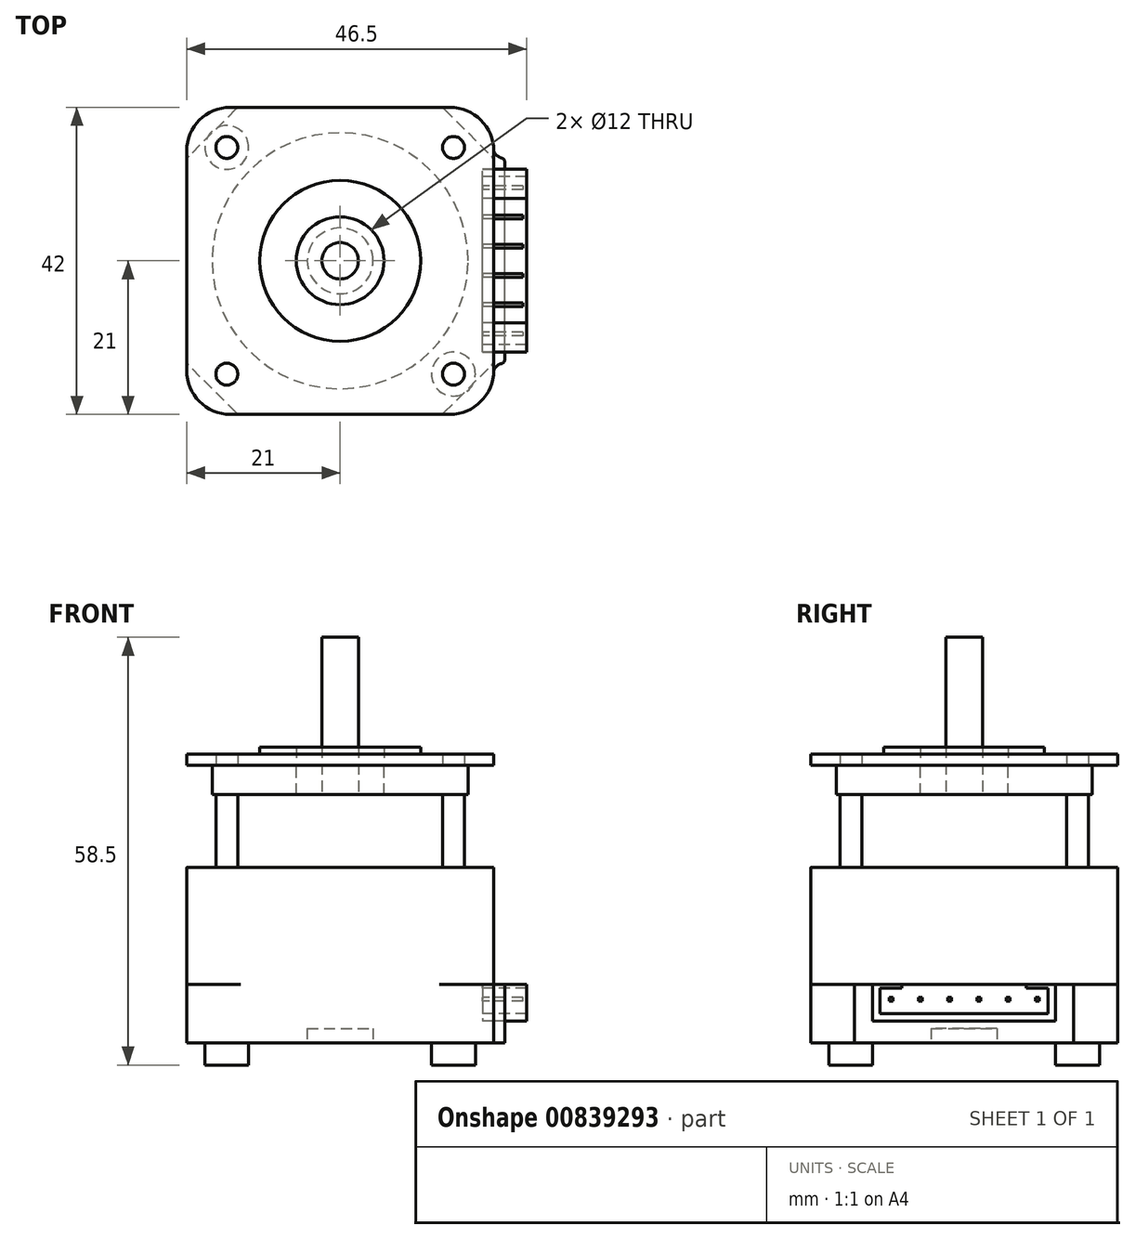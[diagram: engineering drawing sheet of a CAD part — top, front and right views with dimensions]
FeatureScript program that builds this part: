
annotation { "Feature Type Name" : "Feature", "Feature Type Description" : "" }
export const myFeature = defineFeature(function(context is Context, id is Id, definition is map)
    precondition{}
    {
        {
            var Q0;
            Q0=qCreatedBy(makeId("Top.planeOp"),FACE);
            var sketch = newSketch(context, id + "F0", { "sketchPlane" : qUnion([Q0])});
            skLineSegment(sketch, "E0.bottom", {"start": v(21, 21) * mm, "end": v(-21, 21) * mm});
            skLineSegment(sketch, "E0.top", {"start": v(21, -21) * mm, "end": v(-21, -21) * mm});
            skLineSegment(sketch, "E0.left", {"start": v(21, 21) * mm, "end": v(21, -21) * mm});
            skLineSegment(sketch, "E0.right", {"start": v(-21, 21) * mm, "end": v(-21, -21) * mm});
            skPoint(sketch, "E0.middle", {"position": v(0, 0) * mm});
            skLineSegment(sketch, "E1", {"start": v(-14, 21) * mm, "end": v(-21, 14) * mm});
            skLineSegment(sketch, "E2.MirrorCS", {"start": v(14, 21) * mm, "end": v(21, 14) * mm});
            skLineSegment(sketch, "E3.MirrorCS", {"start": v(-14, -21) * mm, "end": v(-21, -14) * mm});
            skLineSegment(sketch, "E4.MirrorCS", {"start": v(14, -21) * mm, "end": v(21, -14) * mm});
            skSolve(sketch);
        }
        {
            var Q0;
            {var subQ0=sQuery(id+"F0.wireOp",EDGE,"E1");Q0=makeQuery(id+"F0.imprint","IMPRINT",FACE,{"disambiguationData":[TD([[makeQuery(id+"F0.imprint","IMPRINT",EDGE,{"derivedFrom":subQ0}),1.0]])]});}
            extrude(context, id + "F1", {"entities" : qUnion([Q0]), "endBound" : BoundingType.SYMMETRIC, "depth" : 18 * mm, "offsetDistance" : 25 * mm});
        }
        {
            var Q0;
            Q0=makeQuery(id+"F1.opExtrude","SWEPT_EDGE",EDGE,{"disambiguationData":[OSD([sQuery(id+"F0.wireOp",EDGE,"E0.right"),sQuery(id+"F0.wireOp",EDGE,"E3.MirrorCS")])]});
            var Q1;
            Q1=makeQuery(id+"F1.opExtrude","SWEPT_EDGE",EDGE,{"disambiguationData":[OSD([sQuery(id+"F0.wireOp",EDGE,"E0.top"),sQuery(id+"F0.wireOp",EDGE,"E3.MirrorCS")])]});
            var Q2;
            Q2=makeQuery(id+"F1.opExtrude","SWEPT_EDGE",EDGE,{"disambiguationData":[OSD([sQuery(id+"F0.wireOp",EDGE,"E0.top"),sQuery(id+"F0.wireOp",EDGE,"E4.MirrorCS")])]});
            var Q3;
            Q3=makeQuery(id+"F1.opExtrude","SWEPT_EDGE",EDGE,{"disambiguationData":[OSD([sQuery(id+"F0.wireOp",EDGE,"E0.left"),sQuery(id+"F0.wireOp",EDGE,"E4.MirrorCS")])]});
            var Q4;
            Q4=makeQuery(id+"F1.opExtrude","SWEPT_EDGE",EDGE,{"disambiguationData":[OSD([sQuery(id+"F0.wireOp",EDGE,"E0.left"),sQuery(id+"F0.wireOp",EDGE,"E2.MirrorCS")])]});
            var Q5;
            Q5=makeQuery(id+"F1.opExtrude","SWEPT_EDGE",EDGE,{"disambiguationData":[OSD([sQuery(id+"F0.wireOp",EDGE,"E0.bottom"),sQuery(id+"F0.wireOp",EDGE,"E2.MirrorCS")])]});
            var Q6;
            Q6=makeQuery(id+"F1.opExtrude","SWEPT_EDGE",EDGE,{"disambiguationData":[OSD([sQuery(id+"F0.wireOp",EDGE,"E0.bottom"),sQuery(id+"F0.wireOp",EDGE,"E1")])]});
            var Q7;
            Q7=makeQuery(id+"F1.opExtrude","SWEPT_EDGE",EDGE,{"disambiguationData":[OSD([sQuery(id+"F0.wireOp",EDGE,"E0.right"),sQuery(id+"F0.wireOp",EDGE,"E1")])]});
            fillet(context, id + "F2", {"entities" : qUnion([Q0, Q1, Q2, Q3, Q4, Q5, Q6, Q7]), "radius" : 1 * mm, "tangentPropagation" : true, "allowEdgeOverflow" : false});
        }
        {
            var Q0;
            Q0=makeQuery(id+"F1.opExtrude","CAP_FACE",FACE,{"disambiguationData":[OSD([sQuery(id+"F0.wireOp",EDGE,"E0.bottom"),sQuery(id+"F0.wireOp",EDGE,"E0.top"),sQuery(id+"F0.wireOp",EDGE,"E0.left"),sQuery(id+"F0.wireOp",EDGE,"E0.right"),sQuery(id+"F0.wireOp",EDGE,"E1"),sQuery(id+"F0.wireOp",EDGE,"E2.MirrorCS"),sQuery(id+"F0.wireOp",EDGE,"E3.MirrorCS"),sQuery(id+"F0.wireOp",EDGE,"E4.MirrorCS")])],"isStart":true});
            var sketch = newSketch(context, id + "F3", { "sketchPlane" : qUnion([Q0])});
            skLineSegment(sketch, "E5.bottom", {"start": v(-21, 21) * mm, "end": v(21, 21) * mm});
            skLineSegment(sketch, "E5.top", {"start": v(-21, -21) * mm, "end": v(21, -21) * mm});
            skLineSegment(sketch, "E5.left", {"start": v(-21, 21) * mm, "end": v(-21, -21) * mm});
            skLineSegment(sketch, "E5.right", {"start": v(21, 21) * mm, "end": v(21, -21) * mm});
            skPoint(sketch, "E5.middle", {"position": v(0, 0) * mm});
            skLineSegment(sketch, "E6", {"start": v(21, 14) * mm, "end": v(22.5, 14) * mm});
            skLineSegment(sketch, "E7.MirrorCS", {"start": v(21, -14) * mm, "end": v(22.5, -14) * mm});
            skLineSegment(sketch, "E8", {"start": v(22.5, 14) * mm, "end": v(22.5, -14) * mm});
            skArc(sketch, "E9", {"start": v(21, 15) * mm, "mid": v(21.6, 14.27) * mm, "end": v(22.5, 14) * mm});
            skArc(sketch, "E10.MirrorCS", {"start": v(21, -15) * mm, "mid": v(21.6, -14.27) * mm, "end": v(22.5, -14) * mm});
            skSolve(sketch);
        }
        {
            var Q0;
            {var subQ3=sQuery(id+"F0.wireOp",EDGE,"E1");Q0=makeQuery(id+"F3.imprint","IMPRINT",FACE,{"disambiguationData":[TD([[makeQuery(id+"F3.imprint","IMPRINT",EDGE,{"derivedFrom":makeQuery(id+"F1.opExtrude","CAP_EDGE",EDGE,{"disambiguationData":[OSD([subQ3])],"isStart":true})}),-1.0]])]});}
            var Q1;
            {var subQ0=sQuery(id+"F0.wireOp",EDGE,"E2.MirrorCS");Q1=makeQuery(id+"F3.imprint","IMPRINT",FACE,{"disambiguationData":[TD([[makeQuery(id+"F3.imprint","IMPRINT",EDGE,{"derivedFrom":makeQuery(id+"F1.opExtrude","CAP_EDGE",EDGE,{"disambiguationData":[OSD([subQ0])],"isStart":true})}),-1.0]])]});}
            var Q2;
            {var subQ0=sQuery(id+"F0.wireOp",EDGE,"E3.MirrorCS");Q2=makeQuery(id+"F3.imprint","IMPRINT",FACE,{"disambiguationData":[TD([[makeQuery(id+"F3.imprint","IMPRINT",EDGE,{"derivedFrom":makeQuery(id+"F1.opExtrude","CAP_EDGE",EDGE,{"disambiguationData":[OSD([subQ0])],"isStart":true})}),-1.0]])]});}
            var Q3;
            {var subQ0=sQuery(id+"F0.wireOp",EDGE,"E4.MirrorCS");Q3=makeQuery(id+"F3.imprint","IMPRINT",FACE,{"disambiguationData":[TD([[makeQuery(id+"F3.imprint","IMPRINT",EDGE,{"derivedFrom":makeQuery(id+"F1.opExtrude","CAP_EDGE",EDGE,{"disambiguationData":[OSD([subQ0])],"isStart":true})}),1.0]])]});}
            var Q4;
            {var subQ0=sQuery(id+"F0.wireOp",EDGE,"E1");Q4=makeQuery(id+"F3.imprint","IMPRINT",FACE,{"disambiguationData":[TD([[makeQuery(id+"F3.imprint","IMPRINT",EDGE,{"derivedFrom":makeQuery(id+"F1.opExtrude","CAP_EDGE",EDGE,{"disambiguationData":[OSD([subQ0])],"isStart":true})}),1.0]])]});}
            var Q5;
            {var subQ0=sQuery(id+"F3.wireOp",EDGE,"E6");Q5=makeQuery(id+"F3.imprint","IMPRINT",FACE,{"disambiguationData":[TD([[makeQuery(id+"F3.imprint","IMPRINT",EDGE,{"derivedFrom":subQ0}),-1.0]])]});}
            var Q6;
            {var subQ0=sQuery(id+"F3.wireOp",EDGE,"E6");Q6=makeQuery(id+"F3.imprint","IMPRINT",FACE,{"disambiguationData":[TD([[makeQuery(id+"F3.imprint","IMPRINT",EDGE,{"derivedFrom":subQ0}),1.0]])]});}
            var Q7;
            {var subQ0=sQuery(id+"F3.wireOp",EDGE,"E7.MirrorCS");Q7=makeQuery(id+"F3.imprint","IMPRINT",FACE,{"disambiguationData":[TD([[makeQuery(id+"F3.imprint","IMPRINT",EDGE,{"derivedFrom":subQ0}),-1.0]])]});}
            extrude(context, id + "F4", {"entities" : qUnion([Q0, Q1, Q2, Q3, Q4, Q5, Q6, Q7]), "operationType" : NewBodyOperationType.ADD, "depth" : 11 * mm, "offsetDistance" : 25 * mm});
        }
        {
            var Q0;
            Q0=makeQuery(id+"F4.opExtrude","SWEPT_EDGE",EDGE,{"disambiguationData":[OSD([sQuery(id+"F3.wireOp",EDGE,"E5.bottom"),sQuery(id+"F3.wireOp",EDGE,"E5.right")])]});
            var Q1;
            Q1=makeQuery(id+"F4.opExtrude","SWEPT_EDGE",EDGE,{"disambiguationData":[OSD([sQuery(id+"F3.wireOp",EDGE,"E5.top"),sQuery(id+"F3.wireOp",EDGE,"E5.right")])]});
            var Q2;
            Q2=makeQuery(id+"F4.opExtrude","SWEPT_EDGE",EDGE,{"disambiguationData":[OSD([sQuery(id+"F3.wireOp",EDGE,"E5.top"),sQuery(id+"F3.wireOp",EDGE,"E5.left")])]});
            var Q3;
            Q3=makeQuery(id+"F4.opExtrude","SWEPT_EDGE",EDGE,{"disambiguationData":[OSD([sQuery(id+"F3.wireOp",EDGE,"E5.bottom"),sQuery(id+"F3.wireOp",EDGE,"E5.left")])]});
            fillet(context, id + "F5", {"entities" : qUnion([Q0, Q1, Q2, Q3]), "radius" : 6 * mm, "tangentPropagation" : true, "allowEdgeOverflow" : false});
        }
        {
            var Q0;
            Q0=makeQuery(id+"F4.opExtrude","SWEPT_EDGE",EDGE,{"disambiguationData":[OSD([sQuery(id+"F3.wireOp",EDGE,"E6"),sQuery(id+"F3.wireOp",EDGE,"E8"),sQuery(id+"F3.wireOp",EDGE,"E9")])]});
            var Q1;
            Q1=makeQuery(id+"F4.opExtrude","SWEPT_EDGE",EDGE,{"disambiguationData":[OSD([sQuery(id+"F3.wireOp",EDGE,"E7.MirrorCS"),sQuery(id+"F3.wireOp",EDGE,"E8"),sQuery(id+"F3.wireOp",EDGE,"E10.MirrorCS")])]});
            fillet(context, id + "F6", {"entities" : qUnion([Q0, Q1]), "radius" : 0.5 * mm, "tangentPropagation" : true, "allowEdgeOverflow" : false});
        }
        {
            var Q0;
            Q0=makeQuery(id+"F4.opExtrude","CAP_FACE",FACE,{"disambiguationData":[OSD([sQuery(id+"F3.wireOp",EDGE,"E5.bottom"),sQuery(id+"F3.wireOp",EDGE,"E5.top"),sQuery(id+"F3.wireOp",EDGE,"E5.left"),sQuery(id+"F3.wireOp",EDGE,"E5.right"),sQuery(id+"F3.wireOp",EDGE,"E8"),sQuery(id+"F3.wireOp",EDGE,"E9"),sQuery(id+"F3.wireOp",EDGE,"E10.MirrorCS")])],"isStart":false});
            var sketch = newSketch(context, id + "F7", { "sketchPlane" : qUnion([Q0])});
            skCircle(sketch, "E11", {"center": v(0, 0) * mm, "radius": 4.5 * mm});
            skSolve(sketch);
        }
        {
            var Q0;
            Q0=makeQuery(id+"F7.imprint","IMPRINT",FACE,{"disambiguationData":[TD([[makeQuery(id+"F7.imprint","IMPRINT",EDGE,{"derivedFrom":sQuery(id+"F7.wireOp",EDGE,"E11")}),1.0]])]});
            extrude(context, id + "F8", {"entities" : qUnion([Q0]), "operationType" : NewBodyOperationType.REMOVE, "oppositeDirection" : true, "depth" : 5 * mm, "offsetDistance" : 25 * mm});
        }
        {
            var Q0;
            Q0=makeQuery(id+"F4.opExtrude","CAP_FACE",FACE,{"disambiguationData":[OSD([sQuery(id+"F3.wireOp",EDGE,"E5.bottom"),sQuery(id+"F3.wireOp",EDGE,"E5.top"),sQuery(id+"F3.wireOp",EDGE,"E5.left"),sQuery(id+"F3.wireOp",EDGE,"E5.right"),sQuery(id+"F3.wireOp",EDGE,"E8"),sQuery(id+"F3.wireOp",EDGE,"E9"),sQuery(id+"F3.wireOp",EDGE,"E10.MirrorCS")])],"isStart":false});
            var sketch = newSketch(context, id + "F9", { "sketchPlane" : qUnion([Q0])});
            skCircle(sketch, "E12", {"center": v(-15.5, 15.5) * mm, "radius": 3 * mm});
            skCircle(sketch, "E13.MirrorC", {"center": v(-15.5, -15.5) * mm, "radius": 3 * mm});
            skCircle(sketch, "E14.MirrorC", {"center": v(15.5, 15.5) * mm, "radius": 3 * mm});
            skCircle(sketch, "E15.MirrorC", {"center": v(15.5, -15.5) * mm, "radius": 3 * mm});
            skSolve(sketch);
        }
        {
            var Q0;
            Q0=makeQuery(id+"F9.imprint","IMPRINT",FACE,{"disambiguationData":[TD([[makeQuery(id+"F9.imprint","IMPRINT",EDGE,{"derivedFrom":sQuery(id+"F9.wireOp",EDGE,"E14.MirrorC")}),-1.0]])]});
            var Q1;
            Q1=makeQuery(id+"F9.imprint","IMPRINT",FACE,{"disambiguationData":[TD([[makeQuery(id+"F9.imprint","IMPRINT",EDGE,{"derivedFrom":sQuery(id+"F9.wireOp",EDGE,"E15.MirrorC")}),1.0]])]});
            var Q2;
            Q2=makeQuery(id+"F9.imprint","IMPRINT",FACE,{"disambiguationData":[TD([[makeQuery(id+"F9.imprint","IMPRINT",EDGE,{"derivedFrom":sQuery(id+"F9.wireOp",EDGE,"E13.MirrorC")}),-1.0]])]});
            var Q3;
            Q3=makeQuery(id+"F9.imprint","IMPRINT",FACE,{"disambiguationData":[TD([[makeQuery(id+"F9.imprint","IMPRINT",EDGE,{"derivedFrom":sQuery(id+"F9.wireOp",EDGE,"E12")}),1.0]])]});
            extrude(context, id + "F10", {"entities" : qUnion([Q0, Q1, Q2, Q3]), "operationType" : NewBodyOperationType.REMOVE, "oppositeDirection" : true, "depth" : 3 * mm, "offsetDistance" : 25 * mm});
        }
        {
            var Q0;
            Q0=makeQuery(id+"F1.opExtrude","CAP_FACE",FACE,{"disambiguationData":[OSD([sQuery(id+"F0.wireOp",EDGE,"E0.bottom"),sQuery(id+"F0.wireOp",EDGE,"E0.top"),sQuery(id+"F0.wireOp",EDGE,"E0.left"),sQuery(id+"F0.wireOp",EDGE,"E0.right"),sQuery(id+"F0.wireOp",EDGE,"E1"),sQuery(id+"F0.wireOp",EDGE,"E2.MirrorCS"),sQuery(id+"F0.wireOp",EDGE,"E3.MirrorCS"),sQuery(id+"F0.wireOp",EDGE,"E4.MirrorCS")])],"isStart":false});
            var sketch = newSketch(context, id + "F11", { "sketchPlane" : qUnion([Q0])});
            skLineSegment(sketch, "E16.bottom", {"start": v(21, -21) * mm, "end": v(-21, -21) * mm});
            skLineSegment(sketch, "E16.top", {"start": v(21, 21) * mm, "end": v(-21, 21) * mm});
            skLineSegment(sketch, "E16.left", {"start": v(21, -21) * mm, "end": v(21, 21) * mm});
            skLineSegment(sketch, "E16.right", {"start": v(-21, -21) * mm, "end": v(-21, 21) * mm});
            skPoint(sketch, "E16.middle", {"position": v(0, 0) * mm});
            skSolve(sketch);
        }
        {
            var Q0;
            {var subQ3=sQuery(id+"F0.wireOp",EDGE,"E1");Q0=makeQuery(id+"F11.imprint","IMPRINT",FACE,{"disambiguationData":[TD([[makeQuery(id+"F11.imprint","IMPRINT",EDGE,{"derivedFrom":makeQuery(id+"F1.opExtrude","CAP_EDGE",EDGE,{"disambiguationData":[OSD([subQ3])],"isStart":false})}),1.0]])]});}
            var Q1;
            {var subQ0=sQuery(id+"F0.wireOp",EDGE,"E1");Q1=makeQuery(id+"F11.imprint","IMPRINT",FACE,{"disambiguationData":[TD([[makeQuery(id+"F11.imprint","IMPRINT",EDGE,{"derivedFrom":makeQuery(id+"F1.opExtrude","CAP_EDGE",EDGE,{"disambiguationData":[OSD([subQ0])],"isStart":false})}),-1.0]])]});}
            var Q2;
            {var subQ0=sQuery(id+"F0.wireOp",EDGE,"E2.MirrorCS");Q2=makeQuery(id+"F11.imprint","IMPRINT",FACE,{"disambiguationData":[TD([[makeQuery(id+"F11.imprint","IMPRINT",EDGE,{"derivedFrom":makeQuery(id+"F1.opExtrude","CAP_EDGE",EDGE,{"disambiguationData":[OSD([subQ0])],"isStart":false})}),1.0]])]});}
            var Q3;
            {var subQ0=sQuery(id+"F0.wireOp",EDGE,"E4.MirrorCS");Q3=makeQuery(id+"F11.imprint","IMPRINT",FACE,{"disambiguationData":[TD([[makeQuery(id+"F11.imprint","IMPRINT",EDGE,{"derivedFrom":makeQuery(id+"F1.opExtrude","CAP_EDGE",EDGE,{"disambiguationData":[OSD([subQ0])],"isStart":false})}),-1.0]])]});}
            var Q4;
            {var subQ0=sQuery(id+"F0.wireOp",EDGE,"E3.MirrorCS");Q4=makeQuery(id+"F11.imprint","IMPRINT",FACE,{"disambiguationData":[TD([[makeQuery(id+"F11.imprint","IMPRINT",EDGE,{"derivedFrom":makeQuery(id+"F1.opExtrude","CAP_EDGE",EDGE,{"disambiguationData":[OSD([subQ0])],"isStart":false})}),1.0]])]});}
            extrude(context, id + "F12", {"entities" : qUnion([Q0, Q1, Q2, Q3, Q4]), "operationType" : NewBodyOperationType.ADD, "depth" : 8 * mm, "offsetDistance" : 25 * mm});
        }
        {
            var Q0;
            Q0=makeQuery(id+"F12.opExtrude","SWEPT_EDGE",EDGE,{"disambiguationData":[OSD([sQuery(id+"F11.wireOp",EDGE,"E16.bottom"),sQuery(id+"F11.wireOp",EDGE,"E16.right")])]});
            var Q1;
            Q1=makeQuery(id+"F12.opExtrude","SWEPT_EDGE",EDGE,{"disambiguationData":[OSD([sQuery(id+"F11.wireOp",EDGE,"E16.bottom"),sQuery(id+"F11.wireOp",EDGE,"E16.left")])]});
            var Q2;
            Q2=makeQuery(id+"F12.opExtrude","SWEPT_EDGE",EDGE,{"disambiguationData":[OSD([sQuery(id+"F11.wireOp",EDGE,"E16.top"),sQuery(id+"F11.wireOp",EDGE,"E16.left")])]});
            var Q3;
            Q3=makeQuery(id+"F12.opExtrude","SWEPT_EDGE",EDGE,{"disambiguationData":[OSD([sQuery(id+"F11.wireOp",EDGE,"E16.top"),sQuery(id+"F11.wireOp",EDGE,"E16.right")])]});
            fillet(context, id + "F13", {"entities" : qUnion([Q0, Q1, Q2, Q3]), "radius" : 6 * mm, "tangentPropagation" : true, "allowEdgeOverflow" : false});
        }
        {
            var Q0;
            Q0=makeQuery(id+"F12.opExtrude","CAP_FACE",FACE,{"disambiguationData":[OSD([sQuery(id+"F11.wireOp",EDGE,"E16.bottom"),sQuery(id+"F11.wireOp",EDGE,"E16.top"),sQuery(id+"F11.wireOp",EDGE,"E16.left"),sQuery(id+"F11.wireOp",EDGE,"E16.right")])],"isStart":false});
            var sketch = newSketch(context, id + "F14", { "sketchPlane" : qUnion([Q0])});
            skCircle(sketch, "E17", {"center": v(-15.5, 15.5) * mm, "radius": 1.5 * mm});
            skCircle(sketch, "E18.MirrorC", {"center": v(-15.5, -15.5) * mm, "radius": 1.5 * mm});
            skCircle(sketch, "E19.MirrorC", {"center": v(15.5, 15.5) * mm, "radius": 1.5 * mm});
            skCircle(sketch, "E20.MirrorC", {"center": v(15.5, -15.5) * mm, "radius": 1.5 * mm});
            skSolve(sketch);
        }
        {
            var Q0;
            Q0=makeQuery(id+"F14.imprint","IMPRINT",FACE,{"disambiguationData":[TD([[makeQuery(id+"F14.imprint","IMPRINT",EDGE,{"derivedFrom":sQuery(id+"F14.wireOp",EDGE,"E19.MirrorC")}),-1.0]])]});
            var Q1;
            Q1=makeQuery(id+"F14.imprint","IMPRINT",FACE,{"disambiguationData":[TD([[makeQuery(id+"F14.imprint","IMPRINT",EDGE,{"derivedFrom":sQuery(id+"F14.wireOp",EDGE,"E20.MirrorC")}),1.0]])]});
            var Q2;
            Q2=makeQuery(id+"F14.imprint","IMPRINT",FACE,{"disambiguationData":[TD([[makeQuery(id+"F14.imprint","IMPRINT",EDGE,{"derivedFrom":sQuery(id+"F14.wireOp",EDGE,"E18.MirrorC")}),-1.0]])]});
            var Q3;
            Q3=makeQuery(id+"F14.imprint","IMPRINT",FACE,{"disambiguationData":[TD([[makeQuery(id+"F14.imprint","IMPRINT",EDGE,{"derivedFrom":sQuery(id+"F14.wireOp",EDGE,"E17")}),1.0]])]});
            extrude(context, id + "F15", {"entities" : qUnion([Q0, Q1, Q2, Q3]), "operationType" : NewBodyOperationType.REMOVE, "oppositeDirection" : true, "depth" : 10 * mm, "offsetDistance" : 25 * mm});
        }
        {
            var Q0;
            Q0=makeQuery(id+"F12.opExtrude","CAP_FACE",FACE,{"disambiguationData":[OSD([sQuery(id+"F11.wireOp",EDGE,"E16.bottom"),sQuery(id+"F11.wireOp",EDGE,"E16.top"),sQuery(id+"F11.wireOp",EDGE,"E16.left"),sQuery(id+"F11.wireOp",EDGE,"E16.right")])],"isStart":false});
            var sketch = newSketch(context, id + "F16", { "sketchPlane" : qUnion([Q0])});
            skCircle(sketch, "E21", {"center": v(0, 0) * mm, "radius": 17.5 * mm});
            skSolve(sketch);
        }
        {
            var Q0;
            Q0=makeQuery(id+"F16.imprint","IMPRINT",FACE,{"disambiguationData":[TD([[makeQuery(id+"F16.imprint","IMPRINT",EDGE,{"derivedFrom":sQuery(id+"F16.wireOp",EDGE,"E21")}),1.0]])]});
            extrude(context, id + "F17", {"entities" : qUnion([Q0]), "depth" : 4 * mm, "offsetDistance" : 25 * mm});
        }
        {
            var Q0;
            Q0=makeQuery(id+"F17.opExtrude","CAP_FACE",FACE,{"disambiguationData":[OSD([sQuery(id+"F16.wireOp",EDGE,"E21")])],"isStart":false});
            var sketch = newSketch(context, id + "F18", { "sketchPlane" : qUnion([Q0])});
            skCircle(sketch, "E22", {"center": v(0, 0) * mm, "radius": 6 * mm});
            skSolve(sketch);
        }
        {
            var Q0;
            Q0=makeQuery(id+"F18.imprint","IMPRINT",FACE,{"disambiguationData":[TD([[makeQuery(id+"F18.imprint","IMPRINT",EDGE,{"derivedFrom":sQuery(id+"F18.wireOp",EDGE,"E22")}),1.0]])]});
            extrude(context, id + "F19", {"entities" : qUnion([Q0]), "operationType" : NewBodyOperationType.REMOVE, "oppositeDirection" : true, "depth" : 4 * mm, "offsetDistance" : 25 * mm});
        }
        {
            var Q0;
            Q0=makeQuery(id+"F12.opExtrude","CAP_FACE",FACE,{"disambiguationData":[OSD([sQuery(id+"F11.wireOp",EDGE,"E16.bottom"),sQuery(id+"F11.wireOp",EDGE,"E16.top"),sQuery(id+"F11.wireOp",EDGE,"E16.left"),sQuery(id+"F11.wireOp",EDGE,"E16.right")])],"isStart":false});
            var sketch = newSketch(context, id + "F20", { "sketchPlane" : qUnion([Q0])});
            skCircle(sketch, "E23", {"center": v(0, 0) * mm, "radius": 2.5 * mm});
            skSolve(sketch);
        }
        {
            var Q0;
            Q0=makeQuery(id+"F20.imprint","IMPRINT",FACE,{"disambiguationData":[TD([[makeQuery(id+"F20.imprint","IMPRINT",EDGE,{"derivedFrom":sQuery(id+"F20.wireOp",EDGE,"E23")}),1.0]])]});
            extrude(context, id + "F21", {"entities" : qUnion([Q0]), "operationType" : NewBodyOperationType.ADD, "depth" : (58.5 - 37) * mm, "offsetDistance" : 25 * mm});
        }
        {
            var Q0;
            Q0=makeQuery(id+"F17.opExtrude","CAP_FACE",FACE,{"disambiguationData":[OSD([sQuery(id+"F16.wireOp",EDGE,"E21")])],"isStart":false});
            var sketch = newSketch(context, id + "F22", { "sketchPlane" : qUnion([Q0])});
            skLineSegment(sketch, "E24.bottom", {"start": v(-15, -21) * mm, "end": v(15, -21) * mm});
            skLineSegment(sketch, "E24.top", {"start": v(-15, 21) * mm, "end": v(15, 21) * mm});
            skLineSegment(sketch, "E24.left", {"start": v(-21, -15) * mm, "end": v(-21, 15) * mm});
            skLineSegment(sketch, "E24.right", {"start": v(21, -15) * mm, "end": v(21, 15) * mm});
            skPoint(sketch, "E24.middle", {"position": v(0, 0) * mm});
            skPoint(sketch, "E25.visualSharp", {"position": v(21, 21) * mm});
            skArc(sketch, "E25.filletArc", {"start": v(21, 15) * mm, "mid": v(19.24, 19.24) * mm, "end": v(15, 21) * mm});
            skPoint(sketch, "E26.visualSharp", {"position": v(21, -21) * mm});
            skArc(sketch, "E26.filletArc", {"start": v(15, -21) * mm, "mid": v(19.24, -19.24) * mm, "end": v(21, -15) * mm});
            skPoint(sketch, "E27.visualSharp", {"position": v(-21, -21) * mm});
            skArc(sketch, "E27.filletArc", {"start": v(-21, -15) * mm, "mid": v(-19.24, -19.24) * mm, "end": v(-15, -21) * mm});
            skPoint(sketch, "E28.visualSharp", {"position": v(-21, 21) * mm});
            skArc(sketch, "E28.filletArc", {"start": v(-15, 21) * mm, "mid": v(-19.24, 19.24) * mm, "end": v(-21, 15) * mm});
            skCircle(sketch, "E29", {"center": v(-15.5, 15.5) * mm, "radius": 1.5 * mm});
            skCircle(sketch, "E30.MirrorC", {"center": v(-15.5, -15.5) * mm, "radius": 1.5 * mm});
            skCircle(sketch, "E31.MirrorC", {"center": v(15.5, -15.5) * mm, "radius": 1.5 * mm});
            skCircle(sketch, "E32.MirrorC", {"center": v(15.5, 15.5) * mm, "radius": 1.5 * mm});
            skCircle(sketch, "E33", {"center": v(0, 0) * mm, "radius": 6 * mm});
            skSolve(sketch);
        }
        {
            var Q0;
            Q0=makeQuery(id+"F22.imprint","IMPRINT",FACE,{"disambiguationData":[TD([[makeQuery(id+"F22.imprint","IMPRINT",EDGE,{"derivedFrom":sQuery(id+"F22.wireOp",EDGE,"E24.bottom")}),1.0]])]});
            var Q1;
            Q1=makeQuery(id+"F22.imprint","IMPRINT",FACE,{"disambiguationData":[TD([[makeQuery(id+"F22.imprint","IMPRINT",EDGE,{"derivedFrom":sQuery(id+"F22.wireOp",EDGE,"E33")}),-1.0]])]});
            extrude(context, id + "F23", {"entities" : qUnion([Q0, Q1]), "depth" : 1.5 * mm, "offsetDistance" : 25 * mm});
        }
        {
            var Q0;
            Q0=makeQuery(id+"F23.opExtrude","CAP_FACE",FACE,{"disambiguationData":[OSD([sQuery(id+"F22.wireOp",EDGE,"E24.bottom"),sQuery(id+"F22.wireOp",EDGE,"E24.top"),sQuery(id+"F22.wireOp",EDGE,"E24.left"),sQuery(id+"F22.wireOp",EDGE,"E24.right"),sQuery(id+"F22.wireOp",EDGE,"E25.filletArc"),sQuery(id+"F22.wireOp",EDGE,"E26.filletArc"),sQuery(id+"F22.wireOp",EDGE,"E27.filletArc"),sQuery(id+"F22.wireOp",EDGE,"E28.filletArc"),sQuery(id+"F22.wireOp",EDGE,"E29"),sQuery(id+"F22.wireOp",EDGE,"E30.MirrorC"),sQuery(id+"F22.wireOp",EDGE,"E31.MirrorC"),sQuery(id+"F22.wireOp",EDGE,"E32.MirrorC"),sQuery(id+"F22.wireOp",EDGE,"E33")])],"isStart":false});
            var sketch = newSketch(context, id + "F24", { "sketchPlane" : qUnion([Q0])});
            skCircle(sketch, "E34", {"center": v(0, 0) * mm, "radius": 11 * mm});
            skCircle(sketch, "E35", {"center": v(0, 0) * mm, "radius": 6 * mm});
            skSolve(sketch);
        }
        {
            var Q0;
            Q0=makeQuery(id+"F24.imprint","IMPRINT",FACE,{"disambiguationData":[TD([[makeQuery(id+"F24.imprint","IMPRINT",EDGE,{"derivedFrom":sQuery(id+"F24.wireOp",EDGE,"E34")}),1.0]])]});
            extrude(context, id + "F25", {"entities" : qUnion([Q0]), "operationType" : NewBodyOperationType.ADD, "depth" : 1 * mm, "offsetDistance" : 25 * mm});
        }
        {
            var Q0;
            Q0=makeQuery(id+"F4.opExtrude","SWEPT_FACE",FACE,{"disambiguationData":[OSD([sQuery(id+"F3.wireOp",EDGE,"E8")])]});
            var sketch = newSketch(context, id + "F26", { "sketchPlane" : qUnion([Q0])});
            skLineSegment(sketch, "E36.bottom", {"start": v(-12.5, -9) * mm, "end": v(12.5, -9) * mm});
            skLineSegment(sketch, "E36.top", {"start": v(-12.5, -14) * mm, "end": v(12.5, -14) * mm});
            skLineSegment(sketch, "E36.left", {"start": v(-12.5, -9) * mm, "end": v(-12.5, -14) * mm});
            skLineSegment(sketch, "E36.right", {"start": v(12.5, -9) * mm, "end": v(12.5, -14) * mm});
            skSolve(sketch);
        }
        {
            var Q0;
            Q0=makeQuery(id+"F26.imprint","IMPRINT",FACE,{"disambiguationData":[TD([[makeQuery(id+"F26.imprint","IMPRINT",EDGE,{"derivedFrom":sQuery(id+"F26.wireOp",EDGE,"E36.bottom")}),-1.0]])]});
            extrude(context, id + "F27", {"entities" : qUnion([Q0]), "operationType" : NewBodyOperationType.REMOVE, "oppositeDirection" : true, "depth" : 3 * mm, "offsetDistance" : 25 * mm});
        }
        {
            var Q0;
            Q0=makeQuery(id+"F27.boolean.opBoolean","COPY",FACE,{"derivedFrom":makeQuery(id+"F27.opExtrude","CAP_FACE",FACE,{"disambiguationData":[OSD([sQuery(id+"F26.wireOp",EDGE,"E36.bottom"),sQuery(id+"F26.wireOp",EDGE,"E36.top"),sQuery(id+"F26.wireOp",EDGE,"E36.left"),sQuery(id+"F26.wireOp",EDGE,"E36.right")])],"isStart":false})});
            var sketch = newSketch(context, id + "F28", { "sketchPlane" : qUnion([Q0])});
            skLineSegment(sketch, "E37.bottom", {"start": v(-12.5, -9) * mm, "end": v(-8.5, -9) * mm});
            skLineSegment(sketch, "E37.top", {"start": v(-12.5, -14) * mm, "end": v(12.5, -14) * mm});
            skLineSegment(sketch, "E37.left", {"start": v(-12.5, -9) * mm, "end": v(-12.5, -14) * mm});
            skLineSegment(sketch, "E37.right", {"start": v(12.5, -9) * mm, "end": v(12.5, -14) * mm});
            skLineSegment(sketch, "E38.0", {"start": v(-11.5, -9.5) * mm, "end": v(-11.5, -13) * mm});
            skLineSegment(sketch, "E39.0", {"start": v(-11.5, -13) * mm, "end": v(11.5, -13) * mm});
            skLineSegment(sketch, "E40.0", {"start": v(11.5, -9.5) * mm, "end": v(11.5, -13) * mm});
            skLineSegment(sketch, "E41.0", {"start": v(-11.5, -9.5) * mm, "end": v(-8.5, -9.5) * mm});
            skLineSegment(sketch, "E42", {"start": v(-8.5, -9.5) * mm, "end": v(-8.5, -9) * mm});
            skLineSegment(sketch, "E43.MirrorCS", {"start": v(8.5, -9.5) * mm, "end": v(8.5, -9) * mm});
            skLineSegment(sketch, "E44.trimOffspring", {"start": v(8.5, -9.5) * mm, "end": v(11.5, -9.5) * mm});
            skLineSegment(sketch, "E45.trimOffspring", {"start": v(8.5, -9) * mm, "end": v(12.5, -9) * mm});
            skSolve(sketch);
        }
        {
            var Q0;
            Q0=makeQuery(id+"F28.imprint","IMPRINT",FACE,{"disambiguationData":[TD([[makeQuery(id+"F28.imprint","IMPRINT",EDGE,{"derivedFrom":sQuery(id+"F28.wireOp",EDGE,"E37.bottom")}),-1.0]])]});
            extrude(context, id + "F29", {"entities" : qUnion([Q0]), "depth" : 6 * mm, "offsetDistance" : 25 * mm});
        }
        {
            var Q0;
            Q0=makeQuery(id+"F27.boolean.opBoolean","COPY",FACE,{"derivedFrom":makeQuery(id+"F27.opExtrude","CAP_FACE",FACE,{"disambiguationData":[OSD([sQuery(id+"F26.wireOp",EDGE,"E36.bottom"),sQuery(id+"F26.wireOp",EDGE,"E36.top"),sQuery(id+"F26.wireOp",EDGE,"E36.left"),sQuery(id+"F26.wireOp",EDGE,"E36.right")])],"isStart":false})});
            var sketch = newSketch(context, id + "F30", { "sketchPlane" : qUnion([Q0])});
            skLineSegment(sketch, "E46.bottom", {"start": v(-9.75, -11.25) * mm, "end": v(-10.25, -11.25) * mm});
            skLineSegment(sketch, "E46.top", {"start": v(-9.75, -10.75) * mm, "end": v(-10.25, -10.75) * mm});
            skLineSegment(sketch, "E46.left", {"start": v(-9.75, -11.25) * mm, "end": v(-9.75, -10.75) * mm});
            skLineSegment(sketch, "E46.right", {"start": v(-10.25, -11.25) * mm, "end": v(-10.25, -10.75) * mm});
            skPoint(sketch, "E46.middle", {"position": v(-10, -11) * mm});
            skLineSegment(sketch, "E47.1.0.0", {"start": v(-5.75, -11.25) * mm, "end": v(-5.75, -10.75) * mm});
            skLineSegment(sketch, "E47.1.0.1", {"start": v(-5.75, -10.75) * mm, "end": v(-6.25, -10.75) * mm});
            skLineSegment(sketch, "E47.1.0.2", {"start": v(-6.25, -11.25) * mm, "end": v(-6.25, -10.75) * mm});
            skLineSegment(sketch, "E47.1.0.3", {"start": v(-5.75, -11.25) * mm, "end": v(-6.25, -11.25) * mm});
            skLineSegment(sketch, "E47.2.0.0", {"start": v(-1.75, -11.25) * mm, "end": v(-1.75, -10.75) * mm});
            skLineSegment(sketch, "E47.2.0.1", {"start": v(-1.75, -10.75) * mm, "end": v(-2.25, -10.75) * mm});
            skLineSegment(sketch, "E47.2.0.2", {"start": v(-2.25, -11.25) * mm, "end": v(-2.25, -10.75) * mm});
            skLineSegment(sketch, "E47.2.0.3", {"start": v(-1.75, -11.25) * mm, "end": v(-2.25, -11.25) * mm});
            skLineSegment(sketch, "E47.3.0.0", {"start": v(2.25, -11.25) * mm, "end": v(2.25, -10.75) * mm});
            skLineSegment(sketch, "E47.3.0.1", {"start": v(2.25, -10.75) * mm, "end": v(1.75, -10.75) * mm});
            skLineSegment(sketch, "E47.3.0.2", {"start": v(1.75, -11.25) * mm, "end": v(1.75, -10.75) * mm});
            skLineSegment(sketch, "E47.3.0.3", {"start": v(2.25, -11.25) * mm, "end": v(1.75, -11.25) * mm});
            skLineSegment(sketch, "E47.4.0.0", {"start": v(6.25, -11.25) * mm, "end": v(6.25, -10.75) * mm});
            skLineSegment(sketch, "E47.4.0.1", {"start": v(6.25, -10.75) * mm, "end": v(5.75, -10.75) * mm});
            skLineSegment(sketch, "E47.4.0.2", {"start": v(5.75, -11.25) * mm, "end": v(5.75, -10.75) * mm});
            skLineSegment(sketch, "E47.4.0.3", {"start": v(6.25, -11.25) * mm, "end": v(5.75, -11.25) * mm});
            skLineSegment(sketch, "E47.5.0.0", {"start": v(10.25, -11.25) * mm, "end": v(10.25, -10.75) * mm});
            skLineSegment(sketch, "E47.5.0.1", {"start": v(10.25, -10.75) * mm, "end": v(9.75, -10.75) * mm});
            skLineSegment(sketch, "E47.5.0.2", {"start": v(9.75, -11.25) * mm, "end": v(9.75, -10.75) * mm});
            skLineSegment(sketch, "E47.5.0.3", {"start": v(10.25, -11.25) * mm, "end": v(9.75, -11.25) * mm});
            skLineSegment(sketch, "E47.direction1", {"start": v(-9.75, -11.25) * mm, "end": v(-5.75, -11.25) * mm, "construction": true});
            skSolve(sketch);
        }
        {
            var Q0;
            Q0=makeQuery(id+"F30.imprint","IMPRINT",FACE,{"disambiguationData":[TD([[makeQuery(id+"F30.imprint","IMPRINT",EDGE,{"derivedFrom":sQuery(id+"F30.wireOp",EDGE,"E46.bottom")}),-1.0]])]});
            var Q1;
            Q1=makeQuery(id+"F30.imprint","IMPRINT",FACE,{"disambiguationData":[TD([[makeQuery(id+"F30.imprint","IMPRINT",EDGE,{"derivedFrom":sQuery(id+"F30.wireOp",EDGE,"E47.1.0.0")}),1.0]])]});
            var Q2;
            Q2=makeQuery(id+"F30.imprint","IMPRINT",FACE,{"disambiguationData":[TD([[makeQuery(id+"F30.imprint","IMPRINT",EDGE,{"derivedFrom":sQuery(id+"F30.wireOp",EDGE,"E47.2.0.0")}),1.0]])]});
            var Q3;
            Q3=makeQuery(id+"F30.imprint","IMPRINT",FACE,{"disambiguationData":[TD([[makeQuery(id+"F30.imprint","IMPRINT",EDGE,{"derivedFrom":sQuery(id+"F30.wireOp",EDGE,"E47.3.0.0")}),1.0]])]});
            var Q4;
            Q4=makeQuery(id+"F30.imprint","IMPRINT",FACE,{"disambiguationData":[TD([[makeQuery(id+"F30.imprint","IMPRINT",EDGE,{"derivedFrom":sQuery(id+"F30.wireOp",EDGE,"E47.4.0.0")}),1.0]])]});
            var Q5;
            Q5=makeQuery(id+"F30.imprint","IMPRINT",FACE,{"disambiguationData":[TD([[makeQuery(id+"F30.imprint","IMPRINT",EDGE,{"derivedFrom":sQuery(id+"F30.wireOp",EDGE,"E47.5.0.0")}),1.0]])]});
            extrude(context, id + "F31", {"entities" : qUnion([Q0, Q1, Q2, Q3, Q4, Q5]), "operationType" : NewBodyOperationType.ADD, "depth" : 5.5 * mm, "offsetDistance" : 25 * mm});
        }
    });
